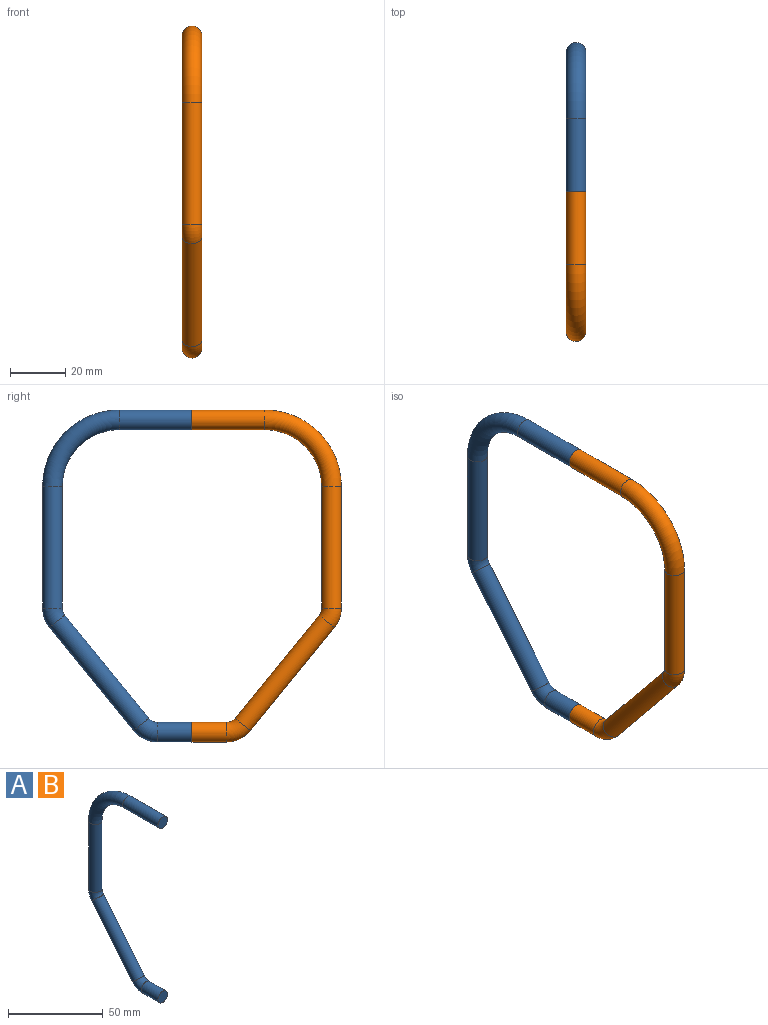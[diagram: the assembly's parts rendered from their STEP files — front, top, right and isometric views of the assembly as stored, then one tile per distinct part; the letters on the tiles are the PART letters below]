
ASSEMBLY  parts=2 mates=1
PART A: 9 faces, bbox 7.1x56.3x123.3 mm
  f0: plane 7.13x7.13mm, normal (0,-1,0), area 39.9mm2, adj f2
  f1: plane 7.13x7.13mm, normal (0,-1,0), area 39.9mm2, adj f8
  f2: cylinder r=3.56mm len=26.35mm, axis (0,1,0), area 589.9mm2, adj f0,f3
  f3: torus R=24.13mm, axis (-1,0,0), area 848.4mm2, adj f2,f4
  f4: cylinder r=3.56mm len=43.95mm, axis (0,0,-1), area 983.7mm2, adj f3,f5
  f5: torus R=7.62mm, axis (-1,0,0), area 116.7mm2, adj f4,f6
  f6: cylinder r=3.56mm len=41.79mm, axis (0,-0.63,-0.77), area 1077.1mm2, adj f5,f7
  f7: torus R=7.62mm, axis (-1,0,0), area 151.2mm2, adj f6,f8
  f8: cylinder r=3.56mm len=12.44mm, axis (0,-1,0), area 278.5mm2, adj f1,f7
PART B: same geometry as A
PLACE A t=(21.88,11.06,-1.62)mm
PLACE B rot(axis=(0,0,-1),180deg) t=(21.88,11.06,-1.62)mm
MATE fastened B.f2 <-> A.f2  axis (0,1,0) through (21.88,11.06,54.49)mm
